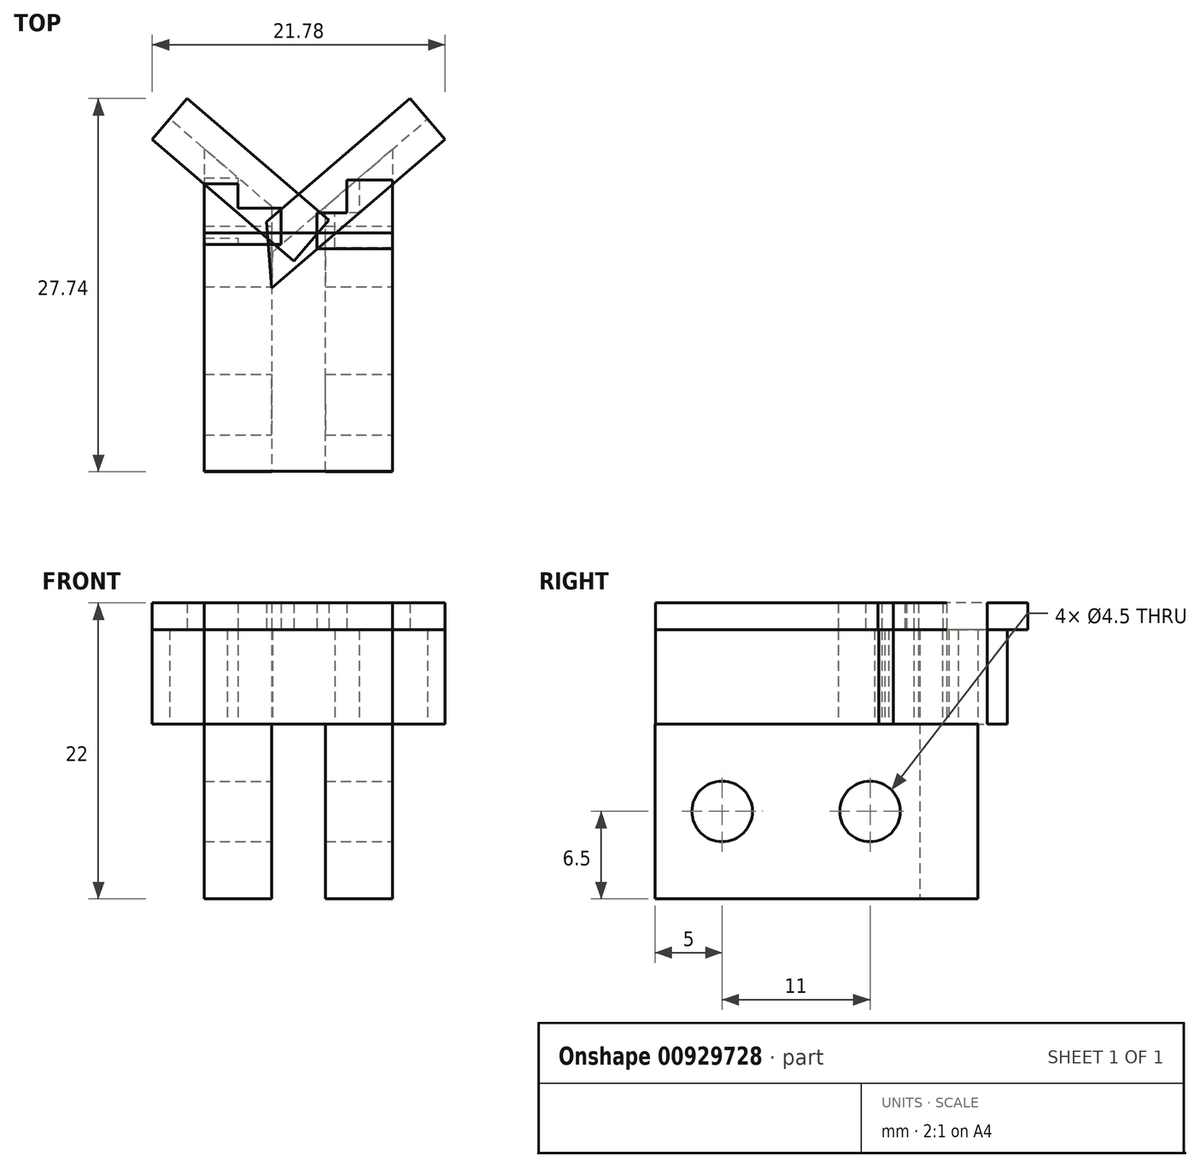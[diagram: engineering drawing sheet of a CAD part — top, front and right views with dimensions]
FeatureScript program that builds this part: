
annotation { "Feature Type Name" : "Feature", "Feature Type Description" : "" }
export const myFeature = defineFeature(function(context is Context, id is Id, definition is map)
    precondition{}
    {
        {
            var Q0;
            Q0=qCreatedBy(makeId("Top.planeOp"),FACE);
            var sketch = newSketch(context, id + "F0", { "sketchPlane" : qUnion([Q0])});
            skLineSegment(sketch, "E0.bottom", {"start": v(-10.6, 13.46) * mm, "end": v(3.4, 13.46) * mm});
            skLineSegment(sketch, "E0.top", {"start": v(-10.6, -10.54) * mm, "end": v(3.4, -10.54) * mm});
            skLineSegment(sketch, "E0.left", {"start": v(-10.6, 13.46) * mm, "end": v(-10.6, -10.54) * mm});
            skLineSegment(sketch, "E0.right", {"start": v(3.4, 13.46) * mm, "end": v(3.4, -10.54) * mm});
            skLineSegment(sketch, "E1", {"start": v(-10.6, -10.54) * mm, "end": v(-10.6, 9.46) * mm});
            skLineSegment(sketch, "E2", {"start": v(3.4, -10.54) * mm, "end": v(3.4, 7.46) * mm});
            skLineSegment(sketch, "E3", {"start": v(3.4, 7.46) * mm, "end": v(-3.6, 7.46) * mm});
            skLineSegment(sketch, "E4", {"start": v(-3.6, 7.46) * mm, "end": v(3.4, 13.46) * mm});
            skLineSegment(sketch, "E5", {"start": v(-3.6, 7.46) * mm, "end": v(-10.6, 13.46) * mm});
            skLineSegment(sketch, "E6", {"start": v(-10.6, 9.46) * mm, "end": v(3.4, 9.46) * mm});
            skLineSegment(sketch, "E7", {"start": v(-10.6, -7.84) * mm, "end": v(-5.6, -7.84) * mm});
            skLineSegment(sketch, "E8", {"start": v(3.4, -7.41) * mm, "end": v(-1.6, -7.41) * mm});
            skLineSegment(sketch, "E9", {"start": v(-5.6, -7.84) * mm, "end": v(-5.6, 9.17) * mm});
            skLineSegment(sketch, "E10", {"start": v(-5.6, -7.84) * mm, "end": v(-5.6, -10.54) * mm});
            skLineSegment(sketch, "E11", {"start": v(-1.6, -7.41) * mm, "end": v(-1.6, 7.46) * mm});
            skLineSegment(sketch, "E12", {"start": v(-1.6, -7.41) * mm, "end": v(-1.6, -10.54) * mm});
            skLineSegment(sketch, "E13", {"start": v(-1.6, 7.46) * mm, "end": v(-1.6, 9.17) * mm});
            skLineSegment(sketch, "E14", {"start": v(-5.6, -10.54) * mm, "end": v(-10.6, -10.54) * mm});
            skLineSegment(sketch, "E15", {"start": v(-1.6, -10.54) * mm, "end": v(3.4, -10.54) * mm});
            skLineSegment(sketch, "E16", {"start": v(-5.6, -10.54) * mm, "end": v(-5.6, -7.84) * mm});
            skLineSegment(sketch, "E17", {"start": v(-5.6, 9.17) * mm, "end": v(-10.6, 13.46) * mm});
            skLineSegment(sketch, "E18", {"start": v(-1.6, 9.17) * mm, "end": v(3.4, 13.46) * mm});
            skSolve(sketch);
        }
        {
            var Q0;
            {var subQ0=sQuery(id+"F0.wireOp",EDGE,"E0.left");Q0=makeQuery(id+"F0.imprint","IMPRINT",FACE,{"disambiguationData":[TD([[makeQuery(id+"F0.imprint","IMPRINT",EDGE,{"derivedFrom":subQ0}),1.0]])]});}
            var Q1;
            {var subQ1=sQuery(id+"F0.wireOp",EDGE,"E0.right");var subQ3=sQuery(id+"F0.wireOp",EDGE,"E6");var subQ4=makeQuery(id+"F0.imprint","INTERSECT",VERTEX,{"derivedFrom":[subQ1,subQ3]});Q1=makeQuery(id+"F0.imprint","IMPRINT",FACE,{"disambiguationData":[TD([[makeQuery(id+"F0.imprint","IMPRINT",EDGE,{"disambiguationData":[TD([[subQ4,1.0]])],"derivedFrom":subQ3}),1.0]])]});}
            var Q2;
            {var subQ0=sQuery(id+"F0.wireOp",EDGE,"E13");Q2=makeQuery(id+"F0.imprint","IMPRINT",FACE,{"disambiguationData":[TD([[makeQuery(id+"F0.imprint","IMPRINT",EDGE,{"derivedFrom":subQ0}),-1.0]])]});}
            var Q3;
            {var subQ3=sQuery(id+"F0.wireOp",EDGE,"E8");Q3=makeQuery(id+"F0.imprint","IMPRINT",FACE,{"disambiguationData":[TD([[makeQuery(id+"F0.imprint","IMPRINT",EDGE,{"derivedFrom":subQ3}),-1.0]])]});}
            var Q4;
            {var subQ2=sQuery(id+"F0.wireOp",EDGE,"E8");Q4=makeQuery(id+"F0.imprint","IMPRINT",FACE,{"disambiguationData":[TD([[makeQuery(id+"F0.imprint","IMPRINT",EDGE,{"derivedFrom":subQ2}),1.0]])]});}
            var Q5;
            {var subQ2=sQuery(id+"F0.wireOp",EDGE,"E7");Q5=makeQuery(id+"F0.imprint","IMPRINT",FACE,{"disambiguationData":[TD([[makeQuery(id+"F0.imprint","IMPRINT",EDGE,{"derivedFrom":subQ2}),-1.0]])]});}
            var Q6;
            {var subQ6=sQuery(id+"F0.wireOp",EDGE,"E7");Q6=makeQuery(id+"F0.imprint","IMPRINT",FACE,{"disambiguationData":[TD([[makeQuery(id+"F0.imprint","IMPRINT",EDGE,{"derivedFrom":subQ6}),1.0]])]});}
            extrude(context, id + "F1", {"entities" : qUnion([Q0, Q1, Q2, Q3, Q4, Q5, Q6]), "depth" : 13 * mm, "offsetDistance" : 25 * mm});
        }
        {
            var Q0;
            Q0=makeQuery(id+"F1.opExtrude","CAP_FACE",FACE,{"disambiguationData":[OSD([sQuery(id+"F0.wireOp",EDGE,"E0.left"),sQuery(id+"F0.wireOp",EDGE,"E1"),sQuery(id+"F0.wireOp",EDGE,"E9"),sQuery(id+"F0.wireOp",EDGE,"E14"),sQuery(id+"F0.wireOp",EDGE,"E16"),sQuery(id+"F0.wireOp",EDGE,"E17")])],"isStart":false});
            var sketch = newSketch(context, id + "F2", { "sketchPlane" : qUnion([Q0])});
            skLineSegment(sketch, "E19", {"start": v(-10.6, 13.46) * mm, "end": v(-1.55, 5.71) * mm});
            skLineSegment(sketch, "E20", {"start": v(-5.6, 9.17) * mm, "end": v(-13.18, 15.68) * mm});
            skLineSegment(sketch, "E21", {"start": v(-13.18, 15.68) * mm, "end": v(-14.48, 14.16) * mm});
            skLineSegment(sketch, "E22", {"start": v(-14.48, 14.16) * mm, "end": v(-1.6, 3.12) * mm});
            skLineSegment(sketch, "E23", {"start": v(-1.55, 5.71) * mm, "end": v(-1.6, 3.12) * mm});
            skSolve(sketch);
        }
        {
            var Q0;
            Q0=makeQuery(id+"F1.opExtrude","CAP_FACE",FACE,{"disambiguationData":[OSD([sQuery(id+"F0.wireOp",EDGE,"E0.right"),sQuery(id+"F0.wireOp",EDGE,"E2"),sQuery(id+"F0.wireOp",EDGE,"E11"),sQuery(id+"F0.wireOp",EDGE,"E13"),sQuery(id+"F0.wireOp",EDGE,"E15"),sQuery(id+"F0.wireOp",EDGE,"E18"),sQuery(id+"F0.wireOp",EDGE,"E12")])],"isStart":false});
            var sketch = newSketch(context, id + "F3", { "sketchPlane" : qUnion([Q0])});
            skLineSegment(sketch, "E24", {"start": v(3.4, 13.46) * mm, "end": v(-5.54, 5.79) * mm});
            skLineSegment(sketch, "E25", {"start": v(-1.6, 9.17) * mm, "end": v(6, 15.68) * mm});
            skLineSegment(sketch, "E26", {"start": v(6, 15.68) * mm, "end": v(7.3, 14.16) * mm});
            skLineSegment(sketch, "E27", {"start": v(-2.8, 8.13) * mm, "end": v(-1.6, 6.54) * mm});
            skLineSegment(sketch, "E28", {"start": v(7.3, 14.16) * mm, "end": v(-5.59, 3.11) * mm});
            skLineSegment(sketch, "E29", {"start": v(-5.54, 5.79) * mm, "end": v(-5.59, 3.11) * mm});
            skLineSegment(sketch, "E30", {"start": v(-5.54, 5.79) * mm, "end": v(6, 15.68) * mm});
            skSolve(sketch);
        }
        {
            var Q0;
            {var subQ3=sQuery(id+"F2.wireOp",EDGE,"E21");Q0=makeQuery(id+"F2.imprint","IMPRINT",FACE,{"disambiguationData":[TD([[makeQuery(id+"F2.imprint","IMPRINT",EDGE,{"derivedFrom":subQ3}),1.0]])]});}
            var sketch = newSketch(context, id + "F4", { "sketchPlane" : qUnion([Q0])});
            skSolve(sketch);
        }
        {
            var Q0;
            {var subQ0=sQuery(id+"F2.wireOp",EDGE,"E19");Q0=makeQuery(id+"F2.imprint","IMPRINT",FACE,{"disambiguationData":[TD([[makeQuery(id+"F2.imprint","IMPRINT",EDGE,{"derivedFrom":subQ0}),-1.0]])]});}
            var Q1;
            {var subQ1=makeQuery(id+"F1.opExtrude","CAP_EDGE",EDGE,{"disambiguationData":[OSD([sQuery(id+"F0.wireOp",EDGE,"E0.left"),sQuery(id+"F0.wireOp",EDGE,"E1")])],"isStart":false});var subQ5=sQuery(id+"F2.wireOp",EDGE,"E22");var subQ6=makeQuery(id+"F2.imprint","INTERSECT",VERTEX,{"derivedFrom":[subQ1,subQ5]});Q1=makeQuery(id+"F2.imprint","IMPRINT",FACE,{"disambiguationData":[TD([[makeQuery(id+"F2.imprint","IMPRINT",EDGE,{"disambiguationData":[TD([[subQ6,-1.0]])],"derivedFrom":subQ5}),1.0]])]});}
            var Q2;
            {var subQ3=sQuery(id+"F2.wireOp",EDGE,"E21");Q2=makeQuery(id+"F4.imprint","IMPRINT",FACE,{"disambiguationData":[TD([[makeQuery(id+"F4.imprint","IMPRINT",EDGE,{"derivedFrom":makeQuery(id+"F2.imprint","IMPRINT",EDGE,{"derivedFrom":subQ3})}),1.0]])]});}
            extrude(context, id + "F5", {"entities" : qUnion([Q0, Q1, Q2]), "depth" : 7 * mm, "offsetDistance" : 25 * mm});
        }
        {
            var Q0;
            Q0=sQuery(id+"F3.wireOp",EDGE,"E28");
            var Q1;
            Q1=sQuery(id+"F3.wireOp",EDGE,"E25");
            var Q2;
            Q2=sQuery(id+"F3.wireOp",EDGE,"E26");
            var Q3;
            Q3=sQuery(id+"F3.wireOp",EDGE,"E24");
            var Q4;
            Q4=sQuery(id+"F3.wireOp",EDGE,"E29");
            extrude(context, id + "F6", {"bodyType" : ToolBodyType.SURFACE, "surfaceEntities" : qUnion([Q0, Q1, Q2, Q3, Q4]), "depth" : 7 * mm, "offsetDistance" : 25 * mm});
        }
        {
            var Q0;
            Q0 = qSketchRegion(id + "F3", true);
            extrude(context, id + "F7", {"entities" : qUnion([Q0]), "depth" : 7 * mm, "offsetDistance" : 25 * mm});
        }
        {
            var Q0;
            Q0=makeQuery(id+"F1.opExtrude","CAP_FACE",FACE,{"disambiguationData":[OSD([sQuery(id+"F0.wireOp",EDGE,"E0.left"),sQuery(id+"F0.wireOp",EDGE,"E1"),sQuery(id+"F0.wireOp",EDGE,"E9"),sQuery(id+"F0.wireOp",EDGE,"E14"),sQuery(id+"F0.wireOp",EDGE,"E16"),sQuery(id+"F0.wireOp",EDGE,"E17")])],"isStart":false});
            var sketch = newSketch(context, id + "F8", { "sketchPlane" : qUnion([Q0])});
            skLineSegment(sketch, "E31.bottom", {"start": v(-10.6, 7.2) * mm, "end": v(3.4, 7.2) * mm});
            skLineSegment(sketch, "E31.top", {"start": v(-10.6, -10.51) * mm, "end": v(3.4, -10.51) * mm});
            skLineSegment(sketch, "E31.left", {"start": v(-10.6, 7.2) * mm, "end": v(-10.6, -10.51) * mm});
            skLineSegment(sketch, "E31.right", {"start": v(3.4, 7.2) * mm, "end": v(3.4, -10.51) * mm});
            skSolve(sketch);
        }
        {
            var Q0;
            {var subQ0=sQuery(id+"F8.wireOp",EDGE,"E31.left");Q0=makeQuery(id+"F8.imprint","IMPRINT",FACE,{"disambiguationData":[TD([[makeQuery(id+"F8.imprint","IMPRINT",EDGE,{"derivedFrom":subQ0}),1.0]])]});}
            var Q1;
            {var subQ0=sQuery(id+"F8.wireOp",EDGE,"E31.right");Q1=makeQuery(id+"F8.imprint","IMPRINT",FACE,{"disambiguationData":[TD([[makeQuery(id+"F8.imprint","IMPRINT",EDGE,{"derivedFrom":subQ0}),-1.0]])]});}
            extrude(context, id + "F9", {"entities" : qUnion([Q0, Q1]), "depth" : 7 * mm, "offsetDistance" : 25 * mm});
        }
        {
            var Q0;
            Q0=makeQuery(id+"F1.opExtrude","CAP_FACE",FACE,{"disambiguationData":[OSD([sQuery(id+"F0.wireOp",EDGE,"E0.left"),sQuery(id+"F0.wireOp",EDGE,"E1"),sQuery(id+"F0.wireOp",EDGE,"E9"),sQuery(id+"F0.wireOp",EDGE,"E14"),sQuery(id+"F0.wireOp",EDGE,"E16"),sQuery(id+"F0.wireOp",EDGE,"E17")])],"isStart":false});
            var sketch = newSketch(context, id + "F10", { "sketchPlane" : qUnion([Q0])});
            skLineSegment(sketch, "E32.bottom", {"start": v(-10.6, 11.32) * mm, "end": v(-8.1, 11.32) * mm});
            skLineSegment(sketch, "E32.top", {"start": v(-10.6, 6.83) * mm, "end": v(-8.1, 6.83) * mm});
            skLineSegment(sketch, "E32.left", {"start": v(-10.6, 11.32) * mm, "end": v(-10.6, 6.83) * mm});
            skLineSegment(sketch, "E32.right", {"start": v(-8.1, 11.32) * mm, "end": v(-8.1, 6.83) * mm});
            skLineSegment(sketch, "E33.bottom", {"start": v(-8.1, 9.07) * mm, "end": v(-5.6, 9.07) * mm});
            skLineSegment(sketch, "E33.top", {"start": v(-8.1, 6.34) * mm, "end": v(-5.6, 6.34) * mm});
            skLineSegment(sketch, "E33.left", {"start": v(-8.1, 9.07) * mm, "end": v(-8.1, 6.34) * mm});
            skLineSegment(sketch, "E33.right", {"start": v(-5.6, 9.07) * mm, "end": v(-5.6, 6.34) * mm});
            skSolve(sketch);
        }
        {
            var Q0;
            Q0 = qSketchRegion(id + "F10", true);
            extrude(context, id + "F11", {"entities" : qUnion([Q0]), "depth" : 7 * mm, "offsetDistance" : 25 * mm});
        }
        {
            var Q0;
            Q0=makeQuery(id+"F1.opExtrude","CAP_FACE",FACE,{"disambiguationData":[OSD([sQuery(id+"F0.wireOp",EDGE,"E0.right"),sQuery(id+"F0.wireOp",EDGE,"E2"),sQuery(id+"F0.wireOp",EDGE,"E11"),sQuery(id+"F0.wireOp",EDGE,"E13"),sQuery(id+"F0.wireOp",EDGE,"E15"),sQuery(id+"F0.wireOp",EDGE,"E18"),sQuery(id+"F0.wireOp",EDGE,"E12")])],"isStart":false});
            var sketch = newSketch(context, id + "F12", { "sketchPlane" : qUnion([Q0])});
            skLineSegment(sketch, "E34.bottom", {"start": v(3.4, 11.16) * mm, "end": v(0.92, 11.16) * mm});
            skLineSegment(sketch, "E34.top", {"start": v(3.4, 6.11) * mm, "end": v(0.92, 6.11) * mm});
            skLineSegment(sketch, "E34.left", {"start": v(3.4, 11.16) * mm, "end": v(3.4, 6.11) * mm});
            skLineSegment(sketch, "E34.right", {"start": v(0.92, 11.16) * mm, "end": v(0.92, 6.11) * mm});
            skLineSegment(sketch, "E35.bottom", {"start": v(0.92, 6.11) * mm, "end": v(-0.9, 6.11) * mm});
            skLineSegment(sketch, "E35.top", {"start": v(0.92, 8.72) * mm, "end": v(-0.9, 8.72) * mm});
            skLineSegment(sketch, "E35.left", {"start": v(0.92, 6.11) * mm, "end": v(0.92, 8.72) * mm});
            skLineSegment(sketch, "E35.right", {"start": v(-0.9, 6.11) * mm, "end": v(-0.9, 8.72) * mm});
            skSolve(sketch);
        }
        {
            var Q0;
            Q0 = qSketchRegion(id + "F12", true);
            extrude(context, id + "F13", {"entities" : qUnion([Q0]), "depth" : 7 * mm, "offsetDistance" : 25 * mm});
        }
        {
            var Q0;
            Q0=makeQuery(id+"F5.opExtrude","CAP_FACE",FACE,{"disambiguationData":[OSD([sQuery(id+"F0.wireOp",EDGE,"E0.left"),sQuery(id+"F0.wireOp",EDGE,"E1"),sQuery(id+"F2.wireOp",EDGE,"E20"),sQuery(id+"F2.wireOp",EDGE,"E21"),sQuery(id+"F2.wireOp",EDGE,"E22")])],"isStart":false});
            var sketch = newSketch(context, id + "F14", { "sketchPlane" : qUnion([Q0])});
            skLineSegment(sketch, "E36", {"start": v(-14.48, 14.16) * mm, "end": v(-11.88, 17.2) * mm});
            skLineSegment(sketch, "E37", {"start": v(-10.6, 10.82) * mm, "end": v(-7.99, 13.86) * mm});
            skLineSegment(sketch, "E38", {"start": v(-11.88, 17.2) * mm, "end": v(-1.34, 8.17) * mm});
            skLineSegment(sketch, "E39", {"start": v(-14.48, 14.16) * mm, "end": v(-3.95, 5.13) * mm});
            skLineSegment(sketch, "E40", {"start": v(-3.95, 5.13) * mm, "end": v(-1.34, 8.17) * mm});
            skLineSegment(sketch, "E41", {"start": v(-1.34, 8.17) * mm, "end": v(-3.95, 5.13) * mm});
            skSolve(sketch);
        }
        {
            var Q0;
            Q0=makeQuery(id+"F7.opExtrude","CAP_FACE",FACE,{"disambiguationData":[OSD([sQuery(id+"F3.wireOp",EDGE,"E26"),sQuery(id+"F3.wireOp",EDGE,"E29"),sQuery(id+"F3.wireOp",EDGE,"E30"),sQuery(id+"F3.wireOp",EDGE,"E28")])],"isStart":false});
            var sketch = newSketch(context, id + "F15", { "sketchPlane" : qUnion([Q0])});
            skLineSegment(sketch, "E42", {"start": v(7.3, 14.16) * mm, "end": v(4.7, 17.2) * mm});
            skLineSegment(sketch, "E43", {"start": v(-0.78, 7.23) * mm, "end": v(-3.38, 10.27) * mm});
            skLineSegment(sketch, "E44", {"start": v(4.7, 17.2) * mm, "end": v(-5.97, 8.05) * mm});
            skLineSegment(sketch, "E45", {"start": v(7.3, 14.16) * mm, "end": v(-5.59, 3.11) * mm});
            skLineSegment(sketch, "E46", {"start": v(-5.59, 3.11) * mm, "end": v(-5.97, 8.05) * mm});
            skSolve(sketch);
        }
        {
            var Q0;
            Q0 = qSketchRegion(id + "F14", true);
            extrude(context, id + "F16", {"entities" : qUnion([Q0]), "depth" : 2 * mm, "offsetDistance" : 25 * mm});
        }
        {
            var Q0;
            Q0 = qSketchRegion(id + "F15", true);
            extrude(context, id + "F17", {"entities" : qUnion([Q0]), "depth" : 2 * mm, "offsetDistance" : 25 * mm});
        }
        {
            var Q0;
            Q0=makeQuery(id+"F9.opExtrude","CAP_FACE",FACE,{"disambiguationData":[OSD([sQuery(id+"F8.wireOp",EDGE,"E31.bottom"),sQuery(id+"F8.wireOp",EDGE,"E31.top"),sQuery(id+"F8.wireOp",EDGE,"E31.left"),sQuery(id+"F8.wireOp",EDGE,"E31.right")])],"isStart":false});
            var sketch = newSketch(context, id + "F18", { "sketchPlane" : qUnion([Q0])});
            skLineSegment(sketch, "E47.bottom", {"start": v(-10.6, 7.2) * mm, "end": v(3.4, 7.2) * mm});
            skLineSegment(sketch, "E47.top", {"start": v(-10.6, -10.51) * mm, "end": v(3.4, -10.51) * mm});
            skLineSegment(sketch, "E47.left", {"start": v(-10.6, 7.2) * mm, "end": v(-10.6, -10.51) * mm});
            skLineSegment(sketch, "E47.right", {"start": v(3.4, 7.2) * mm, "end": v(3.4, -10.51) * mm});
            skSolve(sketch);
        }
        {
            var Q0;
            Q0 = qSketchRegion(id + "F18", true);
            extrude(context, id + "F19", {"entities" : qUnion([Q0]), "depth" : 2 * mm, "offsetDistance" : 25 * mm});
        }
        {
            var Q0;
            Q0=makeQuery(id+"F11.opExtrude","CAP_FACE",FACE,{"disambiguationData":[OSD([sQuery(id+"F10.wireOp",EDGE,"E32.bottom"),sQuery(id+"F10.wireOp",EDGE,"E32.top"),sQuery(id+"F10.wireOp",EDGE,"E32.left"),sQuery(id+"F10.wireOp",EDGE,"E32.right"),sQuery(id+"F10.wireOp",EDGE,"E33.bottom"),sQuery(id+"F10.wireOp",EDGE,"E33.top"),sQuery(id+"F10.wireOp",EDGE,"E33.left"),sQuery(id+"F10.wireOp",EDGE,"E33.right")])],"isStart":false});
            var sketch = newSketch(context, id + "F20", { "sketchPlane" : qUnion([Q0])});
            skLineSegment(sketch, "E48.bottom", {"start": v(-10.6, 9.07) * mm, "end": v(-4.9, 9.07) * mm});
            skLineSegment(sketch, "E48.top", {"start": v(-10.6, 6.34) * mm, "end": v(-4.9, 6.34) * mm});
            skLineSegment(sketch, "E48.left", {"start": v(-10.6, 9.07) * mm, "end": v(-10.6, 6.34) * mm});
            skLineSegment(sketch, "E48.right", {"start": v(-4.9, 9.07) * mm, "end": v(-4.9, 6.34) * mm});
            skLineSegment(sketch, "E49.bottom", {"start": v(-10.6, 9.07) * mm, "end": v(-8.1, 9.07) * mm});
            skLineSegment(sketch, "E49.top", {"start": v(-10.6, 10.88) * mm, "end": v(-8.1, 10.88) * mm});
            skLineSegment(sketch, "E49.left", {"start": v(-10.6, 9.07) * mm, "end": v(-10.6, 10.88) * mm});
            skLineSegment(sketch, "E49.right", {"start": v(-8.1, 9.07) * mm, "end": v(-8.1, 10.88) * mm});
            skSolve(sketch);
        }
        {
            var Q0;
            Q0 = qSketchRegion(id + "F20", true);
            extrude(context, id + "F21", {"entities" : qUnion([Q0]), "depth" : 2 * mm, "offsetDistance" : 25 * mm});
        }
        {
            var Q0;
            Q0=makeQuery(id+"F13.opExtrude","CAP_FACE",FACE,{"disambiguationData":[OSD([sQuery(id+"F12.wireOp",EDGE,"E34.bottom"),sQuery(id+"F12.wireOp",EDGE,"E34.top"),sQuery(id+"F12.wireOp",EDGE,"E34.left"),sQuery(id+"F12.wireOp",EDGE,"E34.right"),sQuery(id+"F12.wireOp",EDGE,"E35.bottom"),sQuery(id+"F12.wireOp",EDGE,"E35.top"),sQuery(id+"F12.wireOp",EDGE,"E35.right")])],"isStart":false});
            var sketch = newSketch(context, id + "F22", { "sketchPlane" : qUnion([Q0])});
            skLineSegment(sketch, "E50.bottom", {"start": v(3.4, 8.72) * mm, "end": v(-2.23, 8.72) * mm});
            skLineSegment(sketch, "E50.top", {"start": v(3.4, 6.04) * mm, "end": v(-2.23, 6.04) * mm});
            skLineSegment(sketch, "E50.left", {"start": v(3.4, 8.72) * mm, "end": v(3.4, 6.04) * mm});
            skLineSegment(sketch, "E50.right", {"start": v(-2.23, 8.72) * mm, "end": v(-2.23, 6.04) * mm});
            skLineSegment(sketch, "E51.bottom", {"start": v(3.4, 8.72) * mm, "end": v(0, 8.72) * mm});
            skLineSegment(sketch, "E51.top", {"start": v(3.4, 11.16) * mm, "end": v(0, 11.16) * mm});
            skLineSegment(sketch, "E51.left", {"start": v(3.4, 8.72) * mm, "end": v(3.4, 11.16) * mm});
            skLineSegment(sketch, "E51.right", {"start": v(0, 8.72) * mm, "end": v(0, 11.16) * mm});
            skSolve(sketch);
        }
        {
            var Q0;
            Q0 = qSketchRegion(id + "F22", true);
            extrude(context, id + "F23", {"entities" : qUnion([Q0]), "depth" : 2 * mm, "offsetDistance" : 25 * mm});
        }
        {
            var Q0;
            Q0=makeQuery(id+"F1.opExtrude","SWEPT_FACE",FACE,{"disambiguationData":[OSD([sQuery(id+"F0.wireOp",EDGE,"E0.right"),sQuery(id+"F0.wireOp",EDGE,"E2")])]});
            var sketch = newSketch(context, id + "F24", { "sketchPlane" : qUnion([Q0])});
            skLineSegment(sketch, "E52", {"start": v(-10.54, 6.5) * mm, "end": v(13.46, 6.5) * mm});
            skLineSegment(sketch, "E53", {"start": v(13.46, 6.5) * mm, "end": v(5.46, 6.5) * mm});
            skLineSegment(sketch, "E54", {"start": v(-10.54, 6.5) * mm, "end": v(-5.54, 6.5) * mm});
            skCircle(sketch, "E55", {"center": v(5.46, 6.5) * mm, "radius": 2 * mm});
            skCircle(sketch, "E56", {"center": v(-5.54, 6.5) * mm, "radius": 2 * mm});
            skSolve(sketch);
        }
        {
            var Q0;
            Q0=sQuery(id+"F24.wireOp",VERTEX,"E54.end");
            var Q1;
            Q1=sQuery(id+"F24.wireOp",VERTEX,"E53.end");
            var Q2;
            Q2=makeQuery(id+"F1.opExtrude","SWEPT_BODY",BODY,{"disambiguationData":[OSD([sQuery(id+"F0.wireOp",EDGE,"E0.left"),sQuery(id+"F0.wireOp",EDGE,"E1"),sQuery(id+"F0.wireOp",EDGE,"E9"),sQuery(id+"F0.wireOp",EDGE,"E14"),sQuery(id+"F0.wireOp",EDGE,"E16"),sQuery(id+"F0.wireOp",EDGE,"E17")])]});
            var Q3;
            Q3=makeQuery(id+"F1.opExtrude","SWEPT_BODY",BODY,{"disambiguationData":[OSD([sQuery(id+"F0.wireOp",EDGE,"E0.right"),sQuery(id+"F0.wireOp",EDGE,"E2"),sQuery(id+"F0.wireOp",EDGE,"E11"),sQuery(id+"F0.wireOp",EDGE,"E13"),sQuery(id+"F0.wireOp",EDGE,"E15"),sQuery(id+"F0.wireOp",EDGE,"E18"),sQuery(id+"F0.wireOp",EDGE,"E12")])]});
            hole(context, id + "F25", {"style" : HoleStyle.SIMPLE, "endStyle" : HoleEndStyle.BLIND_IN_LAST, "holeDiameter" : 4.5 * mm, "tapDrillDiameter" : 4.5 * mm, "majorDiameter" : 5 * mm, "holeDepth" : 14 * mm, "isTappedThrough" : true, "tappedDepth" : 12 * mm, "tapClearance" : 3, "locations" : qUnion([Q0, Q1]), "scope" : qUnion([Q2, Q3])});
        }
    });
